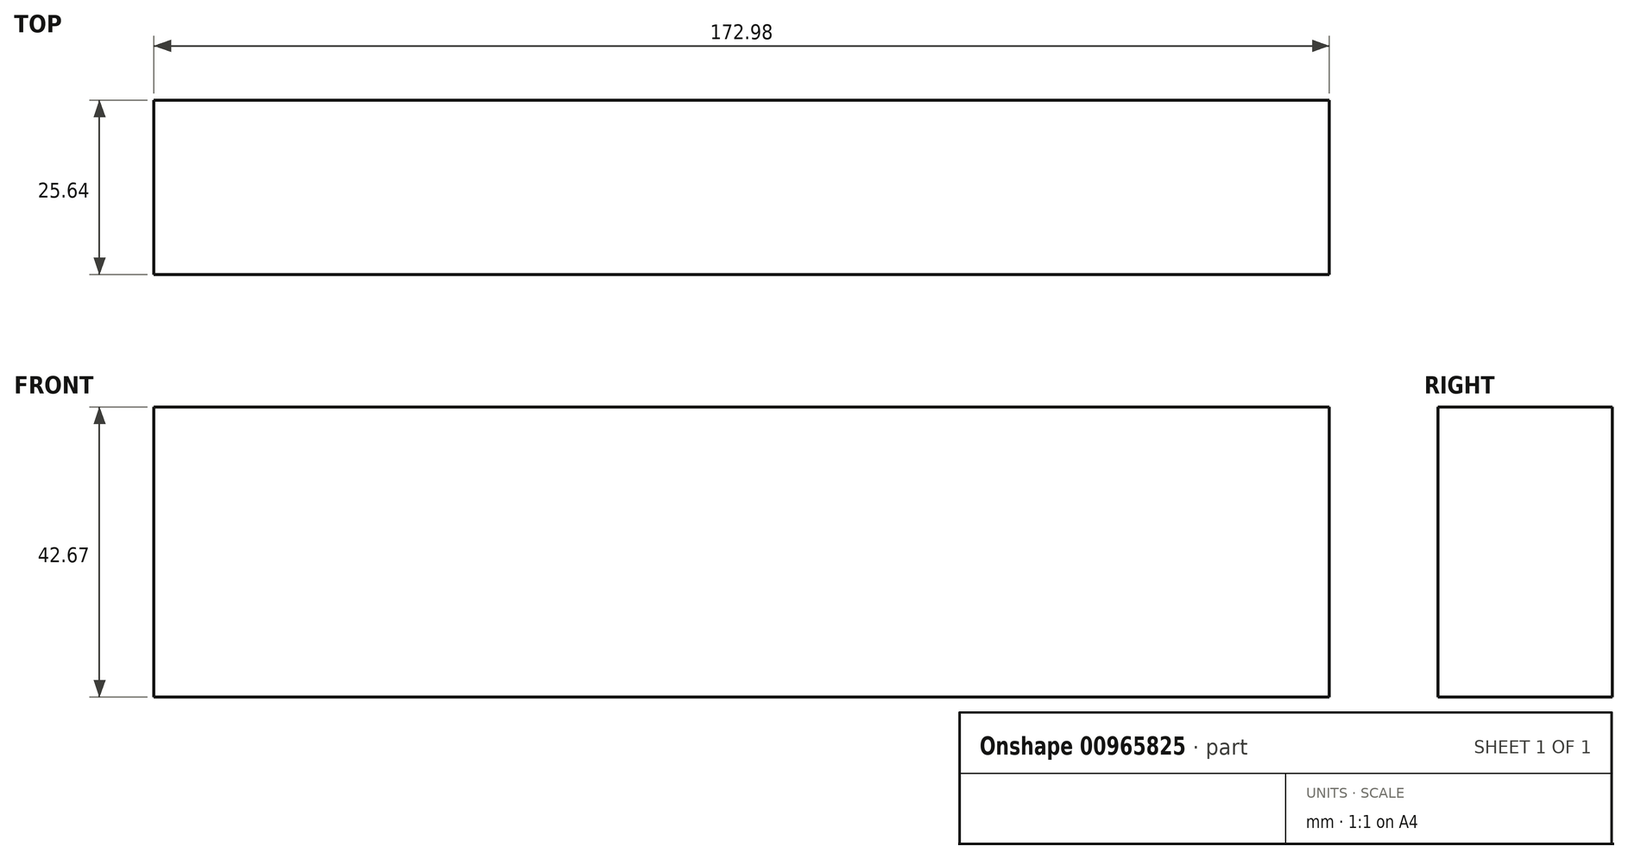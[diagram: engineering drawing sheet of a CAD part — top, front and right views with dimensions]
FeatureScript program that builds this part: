
annotation { "Feature Type Name" : "Feature", "Feature Type Description" : "" }
export const myFeature = defineFeature(function(context is Context, id is Id, definition is map)
    precondition{}
    {
        {
            var Q0;
            Q0=qCreatedBy(makeId("Top.planeOp"),FACE);
            var sketch = newSketch(context, id + "F0", { "sketchPlane" : qUnion([Q0])});
            skLineSegment(sketch, "E0.bottom", {"start": v(-82.07, 0) * mm, "end": v(90.9, 0) * mm});
            skLineSegment(sketch, "E0.top", {"start": v(-82.07, 25.64) * mm, "end": v(90.9, 25.64) * mm});
            skLineSegment(sketch, "E0.left", {"start": v(-82.07, 0) * mm, "end": v(-82.07, 25.64) * mm});
            skLineSegment(sketch, "E0.right", {"start": v(90.9, 0) * mm, "end": v(90.9, 25.64) * mm});
            skLineSegment(sketch, "E1.bottom", {"start": v(0, 0) * mm, "end": v(17.46, 0) * mm});
            skLineSegment(sketch, "E1.top", {"start": v(0, -37.58) * mm, "end": v(17.46, -37.58) * mm});
            skLineSegment(sketch, "E1.left", {"start": v(0, 0) * mm, "end": v(0, -37.58) * mm});
            skLineSegment(sketch, "E1.right", {"start": v(17.46, 0) * mm, "end": v(17.46, -37.58) * mm});
            skSolve(sketch);
        }
        {
            var Q0;
            Q0=makeQuery(id+"F0.imprint","IMPRINT",FACE,{"disambiguationData":[TD([[makeQuery(id+"F0.imprint","IMPRINT",EDGE,{"derivedFrom":sQuery(id+"F0.wireOp",EDGE,"E0.top")}),-1.0]])]});
            extrude(context, id + "F1", {"entities" : qUnion([Q0]), "depth" : 42.67 * mm, "offsetDistance" : 25.4 * mm});
        }
    });
